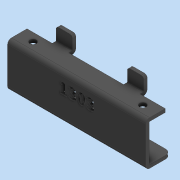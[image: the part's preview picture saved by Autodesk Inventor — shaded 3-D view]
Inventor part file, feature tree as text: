
AUTODESK INVENTOR PART (.ipt)
format: ipt  version: 2020 (Build 240168000, 168)  size: 516,096 bytes
history: native  units: mm
features: other x5, extrude x5, sketch x3, projected_geometry x3, fillet x1
ambient origin geometry x8: Origin, YZ Plane, XZ Plane, XY Plane, X Axis, Y Axis, Z Axis, Center Point
bodies: Body1 (feature_tree)
feature tree (17):
  other  "實體1"
  extrude  "擠出1"  Depth=126.0mm
  extrude  "擠出3"  Depth=20.3mm
  extrude  "擠出4"  Depth=33.0mm
  other  "折彎零件3"
  other  "折彎零件1"
  other  "折彎零件2"
  fillet  "圓角1"  Radius=15.0mm
  extrude  "後加工擴孔"  Depth=3.0mm TaperAngle=0.0deg
  extrude  "後加工倒角"  Depth=0.5mm TaperAngle=90.0deg
  sketch  "草圖3"
  sketch  "草圖4"
  projected_geometry  "投影迴路1"
  sketch  "草圖6"
  projected_geometry  "投影迴路2"
  projected_geometry  "投影迴路3"
  other  "定義1"
